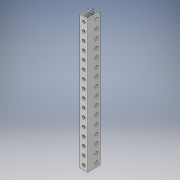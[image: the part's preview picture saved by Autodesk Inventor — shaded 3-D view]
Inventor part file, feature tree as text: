
AUTODESK INVENTOR PART (.ipt)
format: ipt  version: 2019 (Build 230136000, 136)  size: 214,528 bytes
history: native  units: in
note: dims shown in document units (in); Inventor stores cm internally (conversion verified against a paired STEP export)
features: extrude x1, sketch x1, fillet x1
ambient origin geometry x8: Origin, YZ Plane, XZ Plane, XY Plane, X Axis, Y Axis, Z Axis, Center Point
bodies: Solid1 (feature_tree)
feature tree (3):
  extrude  "Extrusion1"  Depth=1.0in
  sketch  "Sketch1"  dims[d0=0.1925in d1=0.1925in d2=1.0in d3=0.0in]
  fillet  "Fillet1"  Radius=1.0in
